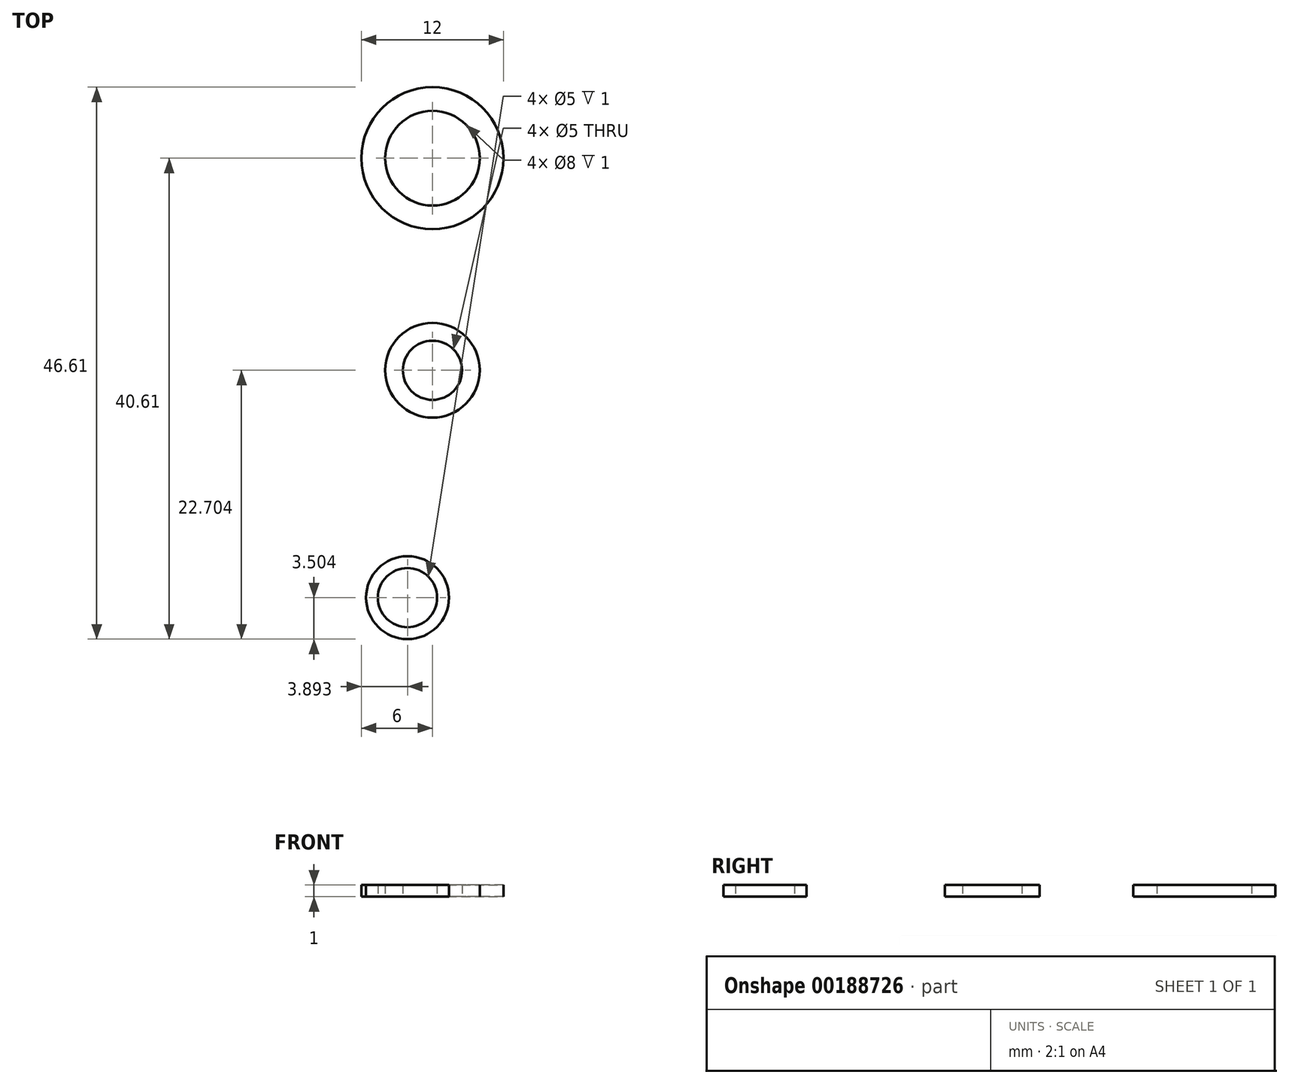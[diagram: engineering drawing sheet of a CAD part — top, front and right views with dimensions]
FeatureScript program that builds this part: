
annotation { "Feature Type Name" : "Feature", "Feature Type Description" : "" }
export const myFeature = defineFeature(function(context is Context, id is Id, definition is map)
    precondition{}
    {
        {
            var Q0;
            Q0=qCreatedBy(makeId("Top.planeOp"),FACE);
            var sketch = newSketch(context, id + "F0", { "sketchPlane" : qUnion([Q0])});
            skCircle(sketch, "E0", {"center": v(0, 0) * mm, "radius": 6 * mm});
            skCircle(sketch, "E1", {"center": v(0, 0) * mm, "radius": 4 * mm});
            skSolve(sketch);
        }
        {
            var Q0;
            Q0=makeQuery(id+"F0.imprint","IMPRINT",FACE,{"disambiguationData":[TD([[makeQuery(id+"F0.imprint","IMPRINT",EDGE,{"derivedFrom":sQuery(id+"F0.wireOp",EDGE,"E0")}),1.0]])]});
            extrude(context, id + "F1", {"entities" : qUnion([Q0]), "depth" : 1 * mm});
        }
        {
            var Q0;
            Q0=qCreatedBy(makeId("Top.planeOp"),FACE);
            var sketch = newSketch(context, id + "F2", { "sketchPlane" : qUnion([Q0])});
            skCircle(sketch, "E2", {"center": v(0, -17.9) * mm, "radius": 4 * mm});
            skCircle(sketch, "E3", {"center": v(0, -17.9) * mm, "radius": 2.5 * mm});
            skSolve(sketch);
        }
        {
            var Q0;
            Q0=makeQuery(id+"F2.imprint","IMPRINT",FACE,{"disambiguationData":[TD([[makeQuery(id+"F2.imprint","IMPRINT",EDGE,{"derivedFrom":sQuery(id+"F2.wireOp",EDGE,"E2")}),1.0]])]});
            extrude(context, id + "F3", {"entities" : qUnion([Q0]), "depth" : 1 * mm});
        }
        {
            var Q0;
            Q0=qCreatedBy(makeId("Top.planeOp"),FACE);
            var sketch = newSketch(context, id + "F4", { "sketchPlane" : qUnion([Q0])});
            skCircle(sketch, "E4", {"center": v(-2.1, -37.1) * mm, "radius": 3.5 * mm});
            skCircle(sketch, "E5", {"center": v(-2.1, -37.1) * mm, "radius": 2.5 * mm});
            skSolve(sketch);
        }
        {
            var Q0;
            Q0=makeQuery(id+"F4.imprint","IMPRINT",FACE,{"disambiguationData":[TD([[makeQuery(id+"F4.imprint","IMPRINT",EDGE,{"derivedFrom":sQuery(id+"F4.wireOp",EDGE,"E4")}),1.0]])]});
            extrude(context, id + "F5", {"entities" : qUnion([Q0]), "depth" : 1 * mm});
        }
    });
